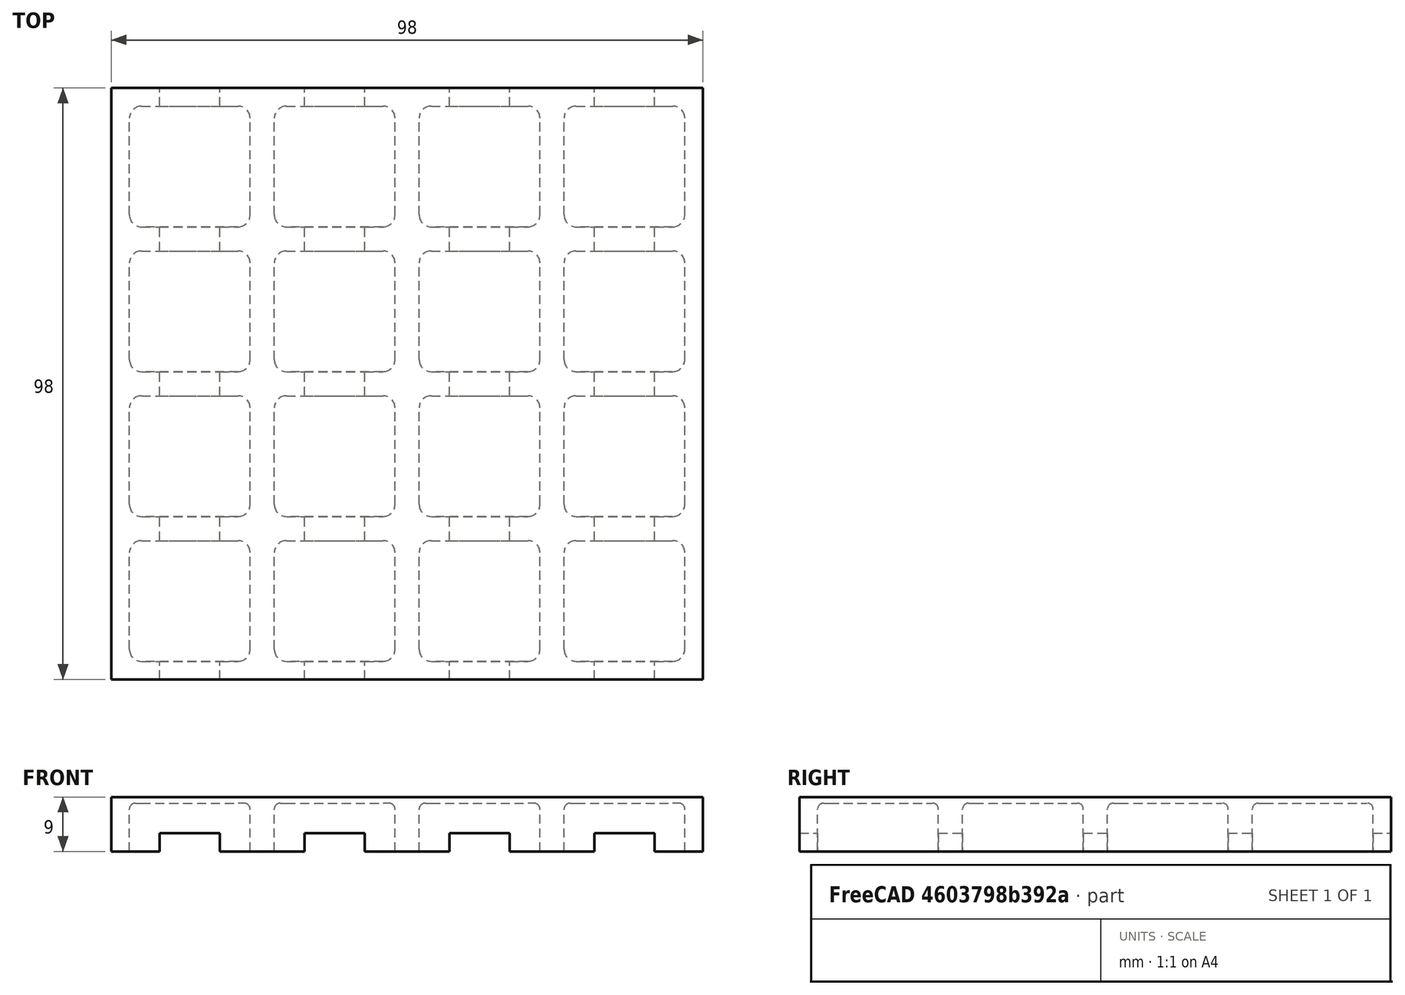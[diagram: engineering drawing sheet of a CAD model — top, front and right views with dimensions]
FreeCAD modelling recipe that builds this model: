
FCSTD DOCUMENT  (FreeCAD 0.16R6700 (Git))
Label: parametric_pad_mold
License: All rights reserved
LicenseURL: http://en.wikipedia.org/wiki/All_rights_reserved
objects: Part::Box×3, Part::Fillet×2, Part::FeaturePython×2, Part::Cut×2, Spreadsheet::Sheet×1
note: 9 computed .brp shape members not serialized (recipe doc carries the construction recipe); baked Part::Feature solids carry a one-line shape summary decoded from their .brp

FEATURE [Spreadsheet::Sheet] Spreadsheet  label="data"
  cells = A2=Button safe height; B2(button_safe_height)=4.6; C2=Pad size; D2(pad_size)=20; A3=N rows pad; B3(rows_pad)=4; A4=N columns pad; B4(columns_pad)=4; A5=Space between pads; B5(space_between_pads)=4; A6=Border; B6(border)=3; A7=Shell; B7(shell)=2; A9=Electronics length; B9(electronics_length)=103; A10=Electronics width; B10(electronics_width)=22
FEATURE [Part::Box] Box008  label="Cube007"
  Height = 8
  Length = 20
  Placement = pos=(0,0,7) rot=(0,0,1;0rad)
  Width = 20
  expr: Width = data.pad_size
  expr: Length = data.pad_size
FEATURE [Part::Fillet] Fillet  label="corners_Fillet"
  Base = -> Box008
  Edges = 4 edges r=2: [Edge1,Edge3,Edge5,Edge7]
FEATURE [Part::Fillet] Fillet001  label="top_Fillet"
  Base = -> Fillet
  Edges = 8 edges r=1: [Edge1,Edge5,Edge6,Edge7,Edge8,Edge9,Edge10,Edge11]
FEATURE [Part::FeaturePython] Array003  label="silicone_pads"  # Draft array (typed FeaturePython)
  Angle = 360
  ArrayType = 0
  Axis = (0,0,1)
  Base = -> Fillet001
  Center = (0,0,0)
  Fuse = false
  IntervalAxis = (0,0,0)
  IntervalX = (24,0,0)
  IntervalY = (0,24,0)
  IntervalZ = (0,0,0)
  NumberPolar = 1
  NumberX = 4
  NumberY = 4
  NumberZ = 1
  expr: NumberY = data.rows_pad
  expr: IntervalX.x = data.space_between_pads + data.pad_size
  expr: NumberX = data.columns_pad
  expr: IntervalY.y = data.space_between_pads + data.pad_size
FEATURE [Part::Box] Box  label="base"
  Height = 9
  Length = 98
  Placement = pos=(-3,-3,7) rot=(0,0,1;0rad)
  Width = 98
  expr: Placement.Base.y = -data.border
  expr: Placement.Base.x = -data.border
  expr: Width = data.rows_pad * data.pad_size + data.space_between_pads * (data.rows_pad - 1) + 2 * data.border
  expr: Length = data.columns_pad * data.pad_size + data.space_between_pads * (data.columns_pad - 1) + 2 * data.border
FEATURE [Part::Cut] Cut  label="base_holed"
  Base = -> Box
  Tool = -> Array003
FEATURE [Part::Box] Box009  label="Cube008"
  Height = 10
  Length = 10
  Placement = pos=(5,-4,0) rot=(0,0,1;0rad)
  Width = 112
  expr: Placement.Base.x = data.pad_size / 2 - 5
  expr: Placement.Base.y = -data.space_between_pads
  expr: Width = data.rows_pad * (data.pad_size + 2 * data.space_between_pads)
FEATURE [Part::FeaturePython] Array  # Draft array (typed FeaturePython)
  Angle = 360
  ArrayType = 0
  Axis = (0,0,1)
  Base = -> Box009
  Center = (0,0,0)
  Fuse = false
  IntervalAxis = (0,0,0)
  IntervalX = (24,0,0)
  IntervalY = (0,1,0)
  IntervalZ = (0,0,0)
  NumberPolar = 4
  NumberX = 4
  NumberY = 1
  NumberZ = 1
  expr: NumberX = data.columns_pad
  expr: IntervalX.x = data.pad_size + data.space_between_pads
  expr: NumberPolar = data.columns_pad
FEATURE [Part::Cut] Cut001  label="parametric_mold"
  Base = -> Cut
  Tool = -> Array
